# Revit family: Steigeleiter Industrie mit C40 Sprosse
name_source: partatom
category: Generic Models
revit_build: Autodesk Revit 2015 (Build: 20140606_1530(x64)
units: mm (PartAtom-declared; Revit-internal decimal feet)

## types (11) — shared parameters
Manufacturer = OBO Bettermann
Material = Steel, Galvanized
URL = http://www.obo-bettermann.com

## per-type parameters (varying)
| type | Article Type | GTIN | Manufacturer Art.No. | Width |
| SLS 80 C40 10 FT | SLS 80 C40 10FT | 4012196011599 | 6013465 | 1000 mm  [stored 3.28084 ft] |
| SLS 80 C40 2 FT | SLS 80 C40 2 FT | 4012196358632 | 6013384 | 200 mm  [stored 0.656168 ft] |
| SLS 80 C40 3 FT | SLS 80 C40 3 FT | 4012196358694 | 6013392 | 300 mm |
| SLS 80 C40 4 FT | SLS 80 C40 4 FT | 4012196011230 | 6013406 | 400 mm  [stored 1.31234 ft] |
| SLS 80 C40 5 FT | SLS 80 C40 5 FT | 4012196011292 | 6013414 | 500 mm  [stored 1.64042 ft] |
| SLS 80 C40 6 FT | SLS 80 C40 6 FT | 4012196011353 | 6013422 | 600 mm |
| SLS 80 C40 7 FT | SLS 80 C40 7 FT | 4012196011414 | 6013430 | 700 mm  [stored 2.29659 ft] |
| SLS 80 C40 8 FT | SLS 80 C40 8 FT | 4012196011476 | 6013449 | 800 mm  [stored 2.62467 ft] |
| SLS 80 C40 9 FT | SLS 80 C40 9 FT | 4012196011537 | 6013457 | 900 mm  [stored 2.95276 ft] |
| SLS 80 C40 11 FT | SLS 80 C40 11FT | 4012196011650 | 6013473 | 1100 mm |
| SLS 80 C40 12 FT | SLS 80 C40 12FT | 4012196011711 | 6013481 | 1200 mm |

note: [stored X ft] marks values corroborated as IEEE doubles in the binary element streams (Revit-internal decimal feet)

## geometry (parser evidence)
native form markers: Sweep x5
no freeform markers — native parametric forms only
